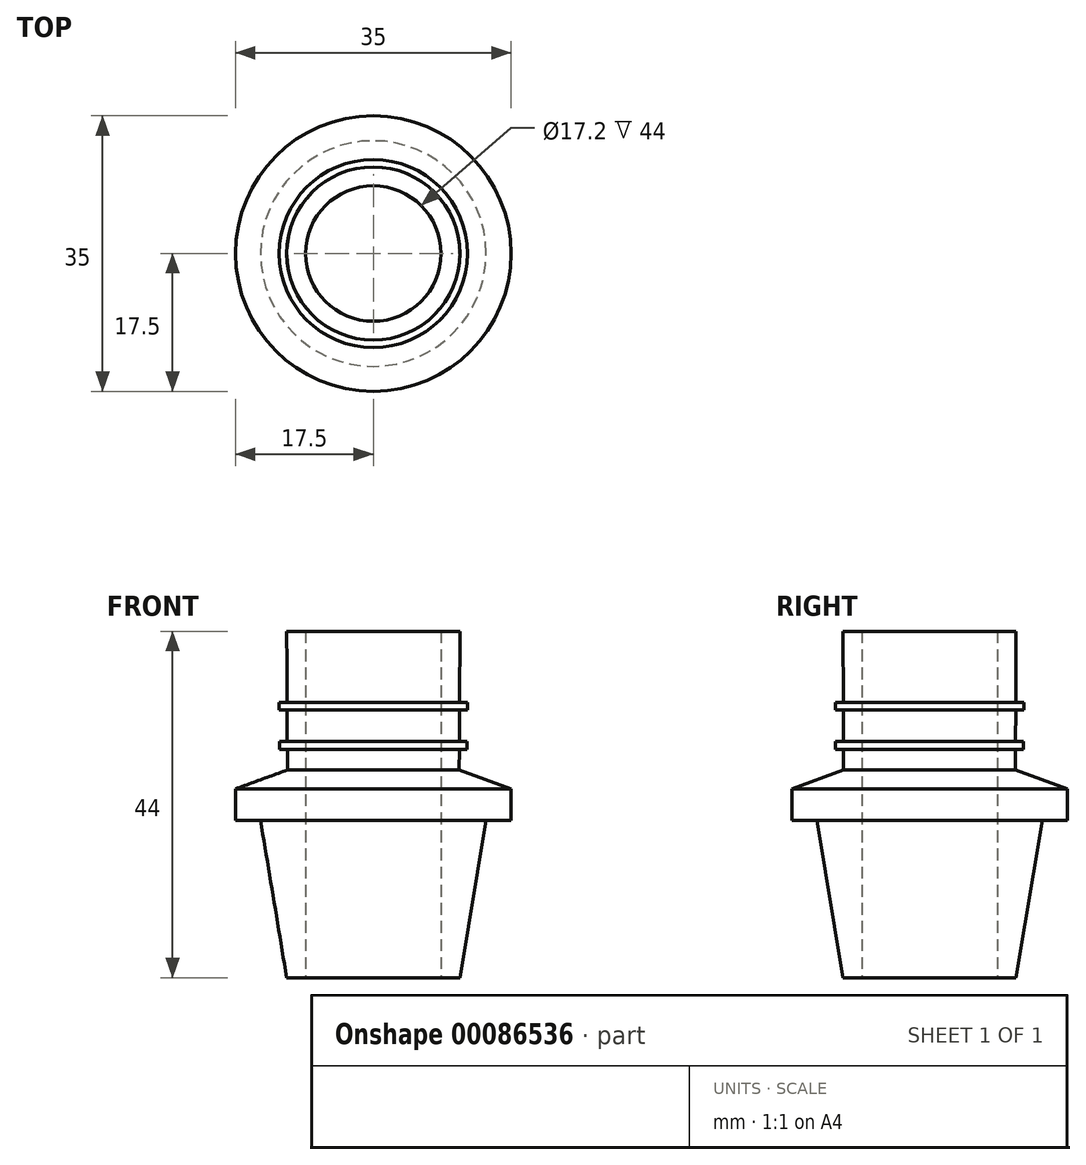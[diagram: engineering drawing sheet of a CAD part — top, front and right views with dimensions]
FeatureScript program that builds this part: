
annotation { "Feature Type Name" : "Feature", "Feature Type Description" : "" }
export const myFeature = defineFeature(function(context is Context, id is Id, definition is map)
    precondition{}
    {
        {
            var Q0;
            Q0=qCreatedBy(makeId("Front.planeOp"),FACE);
            var sketch = newSketch(context, id + "F0", { "sketchPlane" : qUnion([Q0])});
            skLineSegment(sketch, "E0", {"start": v(-17.5, 20) * mm, "end": v(-17.5, 24) * mm});
            skLineSegment(sketch, "E1", {"start": v(-10.9, 24) * mm, "end": v(-11, 44) * mm, "construction": true});
            skLineSegment(sketch, "E2", {"start": v(-11, 44) * mm, "end": v(-8.6, 44) * mm});
            skLineSegment(sketch, "E3", {"start": v(-8.6, 44) * mm, "end": v(-8.6, 0) * mm});
            skLineSegment(sketch, "E4", {"start": v(-8.6, 0) * mm, "end": v(-11, 0) * mm});
            skLineSegment(sketch, "E5", {"start": v(0, 0) * mm, "end": v(0, 21.07) * mm, "construction": true});
            skLineSegment(sketch, "E6", {"start": v(-17.5, 20) * mm, "end": v(-14.33, 20) * mm});
            skLineSegment(sketch, "E7", {"start": v(-10.9, 24) * mm, "end": v(-10.92, 29) * mm});
            skLineSegment(sketch, "E8", {"start": v(-10.92, 29) * mm, "end": v(-11.92, 29) * mm});
            skLineSegment(sketch, "E9", {"start": v(-11.92, 29) * mm, "end": v(-11.92, 30) * mm});
            skLineSegment(sketch, "E10", {"start": v(-11.92, 30) * mm, "end": v(-10.93, 30) * mm});
            skLineSegment(sketch, "E11", {"start": v(-10.93, 30) * mm, "end": v(-10.95, 34) * mm});
            skLineSegment(sketch, "E12", {"start": v(-10.95, 34) * mm, "end": v(-11.95, 34) * mm});
            skLineSegment(sketch, "E13", {"start": v(-11.95, 34) * mm, "end": v(-11.95, 35) * mm});
            skLineSegment(sketch, "E14", {"start": v(-11.95, 35) * mm, "end": v(-10.95, 35) * mm});
            skLineSegment(sketch, "E15", {"start": v(-10.95, 35) * mm, "end": v(-11, 44) * mm});
            skLineSegment(sketch, "E16", {"start": v(-11, 0) * mm, "end": v(-14.33, 20) * mm});
            skLineSegment(sketch, "E17", {"start": v(-17.5, 24) * mm, "end": v(-10.91, 26.4) * mm});
            skSolve(sketch);
        }
        {
            var Q0;
            Q0 = qSketchRegion(id + "F0", true);
            var Q1;
            Q1=sQuery(id+"F0.wireOp",EDGE,"E5");
            revolve(context, id + "F1", {"entities" : qUnion([Q0]), "axis" : qUnion([Q1]), "revolveType" : RevolveType.FULL});
        }
    });
